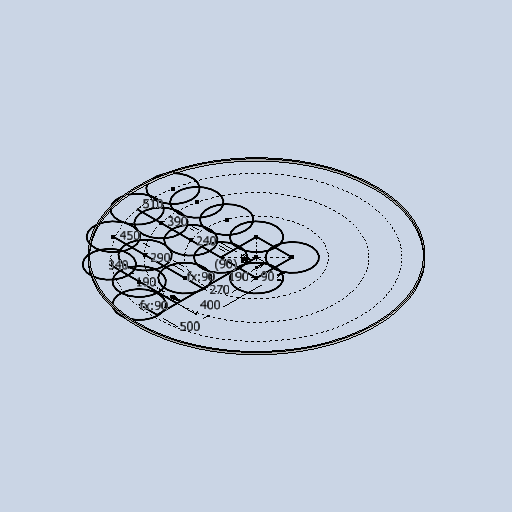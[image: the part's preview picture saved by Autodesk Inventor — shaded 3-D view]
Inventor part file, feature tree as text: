
AUTODESK INVENTOR PART (.ipt)
format: ipt  version: 2025 (Build 290162010, 162A)  size: 149,504 bytes
history: native  units: mm
features: sketch x3, extrude x1
ambient origin geometry x8: Origin, YZ Plane, XZ Plane, XY Plane, X Axis, Y Axis, Z Axis, Center Point
bodies: Solid1 (feature_tree)
feature tree (4):
  extrude  "Extrusion1"  Depth=6.0mm
  sketch  "Sketch2"  dims[d2=10.0mm d3=0.0mm]
  sketch  "Sketch3"  dims[d4=190.0mm d7=90.0mm d8=270.0mm d9=400.0mm d10=500.0mm d11=240.0mm d12=390.0mm d13=510.0mm d14=90.0mm d15=90.0mm d16=290.0mm d17=450.0mm d18=190.0mm d19=340.0mm d20=90.0mm d21=190.0mm d22=1200.0mm]
  sketch  "Sketch1"  dims[d0=1200.0mm d1=6.0mm]
